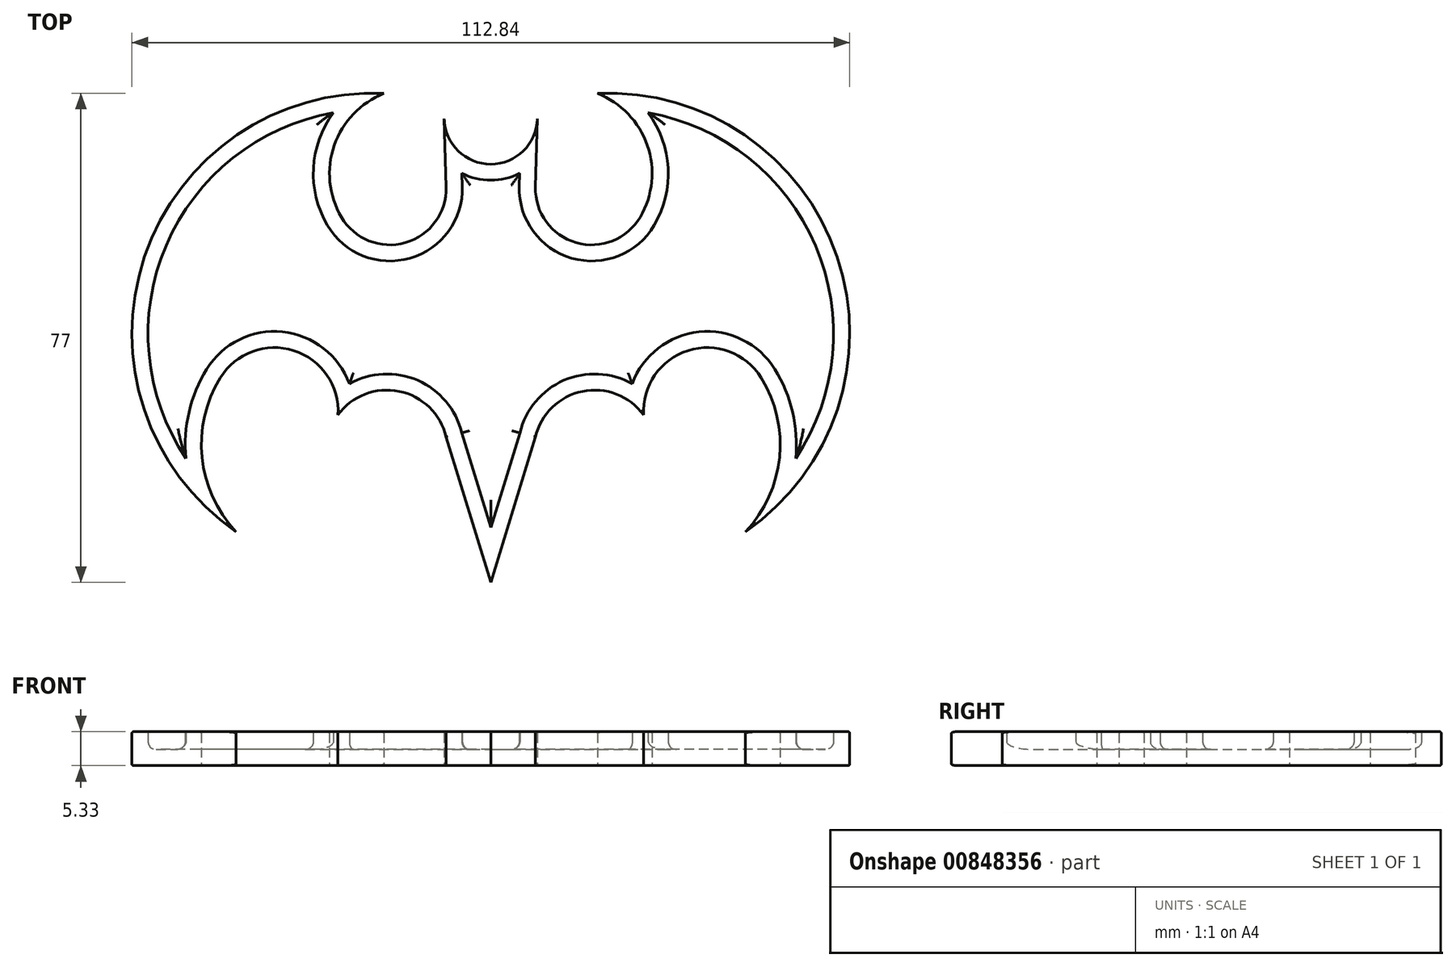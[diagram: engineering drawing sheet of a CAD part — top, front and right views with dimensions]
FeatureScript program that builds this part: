
annotation { "Feature Type Name" : "Feature", "Feature Type Description" : "" }
export const myFeature = defineFeature(function(context is Context, id is Id, definition is map)
    precondition{}
    {
        {
            var Q0;
            Q0=qCreatedBy(makeId("Top.planeOp"),FACE);
            var sketch = newSketch(context, id + "F0", { "sketchPlane" : qUnion([Q0])});
            skArc(sketch, "E0", {"start": v(-7.33, 18.25) * mm, "mid": v(-5.1, 13.2) * mm, "end": v(0, 11.13) * mm});
            skLineSegment(sketch, "E1", {"start": v(-7.33, 18.25) * mm, "end": v(-7.02, 7.53) * mm});
            skArc(sketch, "E2", {"start": v(-7.02, 7.53) * mm, "mid": v(-13.42, -1.23) * mm, "end": v(-23.5, 2.8) * mm});
            skArc(sketch, "E3", {"start": v(-23.5, 2.8) * mm, "mid": v(-24.61, 14.07) * mm, "end": v(-16.78, 22.26) * mm});
            skArc(sketch, "E4", {"start": v(-16.78, 22.26) * mm, "mid": v(-54.44, -3.46) * mm, "end": v(-40.04, -46.73) * mm});
            skArc(sketch, "E5", {"start": v(-42.5, -22.49) * mm, "mid": v(-45.4, -35.02) * mm, "end": v(-40.04, -46.73) * mm});
            skPoint(sketch, "E6.third.point", {"position": v(-25.5, -22.49) * mm});
            skLineSegment(sketch, "E7", {"start": v(-7.02, 7.53) * mm, "end": v(-7.02, 7.02) * mm, "construction": true});
            skArc(sketch, "E8", {"start": v(-7.02, -31.83) * mm, "mid": v(-14.4, -24.63) * mm, "end": v(-24.03, -28.35) * mm});
            skPoint(sketch, "E8.second.point", {"position": v(-7.02, -36.13) * mm});
            skPoint(sketch, "E8.third.point", {"position": v(-15.86, -43.52) * mm});
            skFitSpline(sketch, "E9", {"points": [v(-7.02, -31.83) * mm, v(0, -54.7) * mm], "startDerivative": vector(7.02, -22.88) * mm, "endDerivative": vector(7.02, -22.88) * mm});
            skArc(sketch, "E10.trimOffspring", {"start": v(-24.03, -28.35) * mm, "mid": v(-30.98, -18.22) * mm, "end": v(-42.5, -22.49) * mm});
            skPoint(sketch, "E11", {"position": v(0, 11.13) * mm});
            skArc(sketch, "E12.MirrorCS", {"start": v(7.33, 18.25) * mm, "mid": v(5.1, 13.2) * mm, "end": v(0, 11.13) * mm});
            skLineSegment(sketch, "E13.MirrorCS", {"start": v(7.33, 18.25) * mm, "end": v(7.02, 7.53) * mm});
            skArc(sketch, "E14.MirrorCS", {"start": v(7.02, 7.53) * mm, "mid": v(13.42, -1.23) * mm, "end": v(23.5, 2.8) * mm});
            skArc(sketch, "E15.MirrorCS", {"start": v(23.5, 2.8) * mm, "mid": v(24.61, 14.07) * mm, "end": v(16.78, 22.26) * mm});
            skArc(sketch, "E16.MirrorCS", {"start": v(16.78, 22.26) * mm, "mid": v(54.44, -3.46) * mm, "end": v(40.04, -46.73) * mm});
            skArc(sketch, "E17.MirrorCS", {"start": v(42.5, -22.49) * mm, "mid": v(45.4, -35.02) * mm, "end": v(40.04, -46.73) * mm});
            skArc(sketch, "E18.MirrorCS", {"start": v(24.03, -28.35) * mm, "mid": v(30.98, -18.22) * mm, "end": v(42.5, -22.49) * mm});
            skArc(sketch, "E19.MirrorCS", {"start": v(7.02, -31.83) * mm, "mid": v(14.4, -24.63) * mm, "end": v(24.03, -28.35) * mm});
            skFitSpline(sketch, "E20.MirrorCS", {"points": [v(7.02, -31.83) * mm, v(0, -54.7) * mm], "startDerivative": vector(-7.02, -22.88) * mm, "endDerivative": vector(-7.02, -22.88) * mm});
            skPoint(sketch, "E21.orphan", {"position": v(-15.86, -1.58) * mm});
            skPoint(sketch, "E22.orphan", {"position": v(0, -28.3) * mm});
            skPoint(sketch, "E23.orphan", {"position": v(-7.02, -54.26) * mm});
            skPoint(sketch, "E24.end.orphan", {"position": v(-15.86, -54.26) * mm});
            skSolve(sketch);
        }
        {
            var Q0;
            Q0=qSketchRegion(id+"F0",true);
            extrude(context, id + "F1", {"entities" : qUnion([Q0]), "depth" : 5.33 * mm});
        }
        {
            var Q0;
            Q0=makeQuery(id+"F1.opExtrude","CAP_EDGE",EDGE,{"disambiguationData":[OSD([sQuery(id+"F0.wireOp",EDGE,"E10.trimOffspring")])],"isStart":false});
            var Q1;
            Q1=makeQuery(id+"F1.opExtrude","CAP_FACE",FACE,{"disambiguationData":[OSD([sQuery(id+"F0.wireOp",EDGE,"E0"),sQuery(id+"F0.wireOp",EDGE,"E1"),sQuery(id+"F0.wireOp",EDGE,"E2"),sQuery(id+"F0.wireOp",EDGE,"E3"),sQuery(id+"F0.wireOp",EDGE,"E4"),sQuery(id+"F0.wireOp",EDGE,"E5"),sQuery(id+"F0.wireOp",EDGE,"E8"),sQuery(id+"F0.wireOp",EDGE,"E9"),sQuery(id+"F0.wireOp",EDGE,"E10.trimOffspring"),sQuery(id+"F0.wireOp",EDGE,"E12.MirrorCS"),sQuery(id+"F0.wireOp",EDGE,"E13.MirrorCS"),sQuery(id+"F0.wireOp",EDGE,"E14.MirrorCS"),sQuery(id+"F0.wireOp",EDGE,"E15.MirrorCS"),sQuery(id+"F0.wireOp",EDGE,"E16.MirrorCS"),sQuery(id+"F0.wireOp",EDGE,"E17.MirrorCS"),sQuery(id+"F0.wireOp",EDGE,"E18.MirrorCS"),sQuery(id+"F0.wireOp",EDGE,"E19.MirrorCS"),sQuery(id+"F0.wireOp",EDGE,"E20.MirrorCS")])],"isStart":false});
            fillet(context, id + "F2", {"entities" : qUnion([Q0, Q1]), "radius" : 0.25 * mm, "tangentPropagation" : true, "allowEdgeOverflow" : false});
        }
        {
            var Q0;
            Q0=makeQuery(id+"F1.opExtrude","CAP_FACE",FACE,{"disambiguationData":[OSD([sQuery(id+"F0.wireOp",EDGE,"E0"),sQuery(id+"F0.wireOp",EDGE,"E1"),sQuery(id+"F0.wireOp",EDGE,"E2"),sQuery(id+"F0.wireOp",EDGE,"E3"),sQuery(id+"F0.wireOp",EDGE,"E4"),sQuery(id+"F0.wireOp",EDGE,"E5"),sQuery(id+"F0.wireOp",EDGE,"E8"),sQuery(id+"F0.wireOp",EDGE,"E9"),sQuery(id+"F0.wireOp",EDGE,"E10.trimOffspring"),sQuery(id+"F0.wireOp",EDGE,"E12.MirrorCS"),sQuery(id+"F0.wireOp",EDGE,"E13.MirrorCS"),sQuery(id+"F0.wireOp",EDGE,"E14.MirrorCS"),sQuery(id+"F0.wireOp",EDGE,"E15.MirrorCS"),sQuery(id+"F0.wireOp",EDGE,"E16.MirrorCS"),sQuery(id+"F0.wireOp",EDGE,"E17.MirrorCS"),sQuery(id+"F0.wireOp",EDGE,"E18.MirrorCS"),sQuery(id+"F0.wireOp",EDGE,"E19.MirrorCS"),sQuery(id+"F0.wireOp",EDGE,"E20.MirrorCS")])],"isStart":true});
            fillet(context, id + "F3", {"entities" : qUnion([Q0]), "radius" : 0.25 * mm, "tangentPropagation" : true, "allowEdgeOverflow" : false});
        }
        {
            var Q0;
            Q0=makeQuery(id+"F1.opExtrude","CAP_FACE",FACE,{"disambiguationData":[OSD([sQuery(id+"F0.wireOp",EDGE,"E0"),sQuery(id+"F0.wireOp",EDGE,"E1"),sQuery(id+"F0.wireOp",EDGE,"E2"),sQuery(id+"F0.wireOp",EDGE,"E3"),sQuery(id+"F0.wireOp",EDGE,"E4"),sQuery(id+"F0.wireOp",EDGE,"E5"),sQuery(id+"F0.wireOp",EDGE,"E8"),sQuery(id+"F0.wireOp",EDGE,"E9"),sQuery(id+"F0.wireOp",EDGE,"E10.trimOffspring"),sQuery(id+"F0.wireOp",EDGE,"E12.MirrorCS"),sQuery(id+"F0.wireOp",EDGE,"E13.MirrorCS"),sQuery(id+"F0.wireOp",EDGE,"E14.MirrorCS"),sQuery(id+"F0.wireOp",EDGE,"E15.MirrorCS"),sQuery(id+"F0.wireOp",EDGE,"E16.MirrorCS"),sQuery(id+"F0.wireOp",EDGE,"E17.MirrorCS"),sQuery(id+"F0.wireOp",EDGE,"E18.MirrorCS"),sQuery(id+"F0.wireOp",EDGE,"E19.MirrorCS"),sQuery(id+"F0.wireOp",EDGE,"E20.MirrorCS")])],"isStart":false});
            shell(context, id + "F4", {"entities" : qUnion([Q0]), "thickness" : 2.54 * mm});
        }
        {
            var Q0;
            {var subQ0=sQuery(id+"F0.wireOp",EDGE,"E3");var subQ1=makeQuery(id+"F1.opExtrude","CAP_EDGE",EDGE,{"disambiguationData":[OSD([subQ0])],"isStart":true});var subQ2=sQuery(id+"F0.wireOp",EDGE,"E20.MirrorCS");var subQ3=sQuery(id+"F0.wireOp",EDGE,"E19.MirrorCS");var subQ4=sQuery(id+"F0.wireOp",EDGE,"E18.MirrorCS");var subQ5=sQuery(id+"F0.wireOp",EDGE,"E17.MirrorCS");var subQ6=sQuery(id+"F0.wireOp",EDGE,"E16.MirrorCS");var subQ7=sQuery(id+"F0.wireOp",EDGE,"E15.MirrorCS");var subQ8=sQuery(id+"F0.wireOp",EDGE,"E14.MirrorCS");var subQ9=sQuery(id+"F0.wireOp",EDGE,"E13.MirrorCS");var subQ10=sQuery(id+"F0.wireOp",EDGE,"E12.MirrorCS");var subQ11=sQuery(id+"F0.wireOp",EDGE,"E10.trimOffspring");var subQ12=sQuery(id+"F0.wireOp",EDGE,"E9");var subQ13=sQuery(id+"F0.wireOp",EDGE,"E8");var subQ14=sQuery(id+"F0.wireOp",EDGE,"E5");var subQ15=sQuery(id+"F0.wireOp",EDGE,"E4");var subQ16=sQuery(id+"F0.wireOp",EDGE,"E2");var subQ17=sQuery(id+"F0.wireOp",EDGE,"E1");var subQ18=sQuery(id+"F0.wireOp",EDGE,"E0");Q0=makeQuery(id+"F4.opShell","OFFSET_EDGE",EDGE,{"disambiguationData":[OSD([subQ18,subQ17,subQ16,subQ0,subQ15,subQ14,subQ13,subQ12,subQ11,subQ10,subQ9,subQ8,subQ7,subQ6,subQ5,subQ4,subQ3,subQ2]),TDD([makeQuery(id+"F3.opFillet","BLEND_EDGE",EDGE,{"blendedFrom":[subQ1,makeQuery(id+"F1.opExtrude","CAP_FACE",FACE,{"disambiguationData":[OSD([subQ18,subQ17,subQ16,subQ0,subQ15,subQ14,subQ13,subQ12,subQ11,subQ10,subQ9,subQ8,subQ7,subQ6,subQ5,subQ4,subQ3,subQ2])],"isStart":true})],"blendedInto":[makeQuery(id+"F1.opExtrude","CAP_FACE",FACE,{"disambiguationData":[OSD([subQ18,subQ17,subQ16,subQ0,subQ15,subQ14,subQ13,subQ12,subQ11,subQ10,subQ9,subQ8,subQ7,subQ6,subQ5,subQ4,subQ3,subQ2])],"isStart":true})]}),makeQuery(id+"F3.opFillet","BLEND_EDGE",EDGE,{"blendedFrom":[subQ1,makeQuery(id+"F1.opExtrude","SWEPT_FACE",FACE,{"disambiguationData":[OSD([subQ0])]})],"blendedInto":[makeQuery(id+"F1.opExtrude","SWEPT_FACE",FACE,{"disambiguationData":[OSD([subQ0])]})]})])]});}
            var Q1;
            {var subQ0=sQuery(id+"F0.wireOp",EDGE,"E12.MirrorCS");var subQ1=sQuery(id+"F0.wireOp",EDGE,"E0");var subQ2=makeQuery(id+"F1.opExtrude","CAP_EDGE",EDGE,{"disambiguationData":[OSD([subQ1,subQ0])],"isStart":true});var subQ3=sQuery(id+"F0.wireOp",EDGE,"E20.MirrorCS");var subQ4=sQuery(id+"F0.wireOp",EDGE,"E19.MirrorCS");var subQ5=sQuery(id+"F0.wireOp",EDGE,"E18.MirrorCS");var subQ6=sQuery(id+"F0.wireOp",EDGE,"E17.MirrorCS");var subQ7=sQuery(id+"F0.wireOp",EDGE,"E16.MirrorCS");var subQ8=sQuery(id+"F0.wireOp",EDGE,"E15.MirrorCS");var subQ9=sQuery(id+"F0.wireOp",EDGE,"E14.MirrorCS");var subQ10=sQuery(id+"F0.wireOp",EDGE,"E13.MirrorCS");var subQ11=sQuery(id+"F0.wireOp",EDGE,"E10.trimOffspring");var subQ12=sQuery(id+"F0.wireOp",EDGE,"E9");var subQ13=sQuery(id+"F0.wireOp",EDGE,"E8");var subQ14=sQuery(id+"F0.wireOp",EDGE,"E5");var subQ15=sQuery(id+"F0.wireOp",EDGE,"E4");var subQ16=sQuery(id+"F0.wireOp",EDGE,"E3");var subQ17=sQuery(id+"F0.wireOp",EDGE,"E2");var subQ18=sQuery(id+"F0.wireOp",EDGE,"E1");Q1=makeQuery(id+"F4.opShell","OFFSET_EDGE",EDGE,{"disambiguationData":[OSD([subQ1,subQ18,subQ17,subQ16,subQ15,subQ14,subQ13,subQ12,subQ11,subQ0,subQ10,subQ9,subQ8,subQ7,subQ6,subQ5,subQ4,subQ3]),TDD([makeQuery(id+"F3.opFillet","BLEND_EDGE",EDGE,{"blendedFrom":[subQ2,makeQuery(id+"F1.opExtrude","CAP_FACE",FACE,{"disambiguationData":[OSD([subQ1,subQ18,subQ17,subQ16,subQ15,subQ14,subQ13,subQ12,subQ11,subQ0,subQ10,subQ9,subQ8,subQ7,subQ6,subQ5,subQ4,subQ3])],"isStart":true})],"blendedInto":[makeQuery(id+"F1.opExtrude","CAP_FACE",FACE,{"disambiguationData":[OSD([subQ1,subQ18,subQ17,subQ16,subQ15,subQ14,subQ13,subQ12,subQ11,subQ0,subQ10,subQ9,subQ8,subQ7,subQ6,subQ5,subQ4,subQ3])],"isStart":true})]}),makeQuery(id+"F3.opFillet","BLEND_EDGE",EDGE,{"blendedFrom":[subQ2,makeQuery(id+"F1.opExtrude","SWEPT_FACE",FACE,{"disambiguationData":[OSD([subQ1,subQ0])]})],"blendedInto":[makeQuery(id+"F1.opExtrude","SWEPT_FACE",FACE,{"disambiguationData":[OSD([subQ1,subQ0])]})]})])]});}
            var Q2;
            Q2=makeQuery(id+"F4.opShell","OFFSET_FACE",FACE,{"disambiguationData":[OSD([sQuery(id+"F0.wireOp",EDGE,"E0"),sQuery(id+"F0.wireOp",EDGE,"E1"),sQuery(id+"F0.wireOp",EDGE,"E2"),sQuery(id+"F0.wireOp",EDGE,"E3"),sQuery(id+"F0.wireOp",EDGE,"E4"),sQuery(id+"F0.wireOp",EDGE,"E5"),sQuery(id+"F0.wireOp",EDGE,"E8"),sQuery(id+"F0.wireOp",EDGE,"E9"),sQuery(id+"F0.wireOp",EDGE,"E10.trimOffspring"),sQuery(id+"F0.wireOp",EDGE,"E12.MirrorCS"),sQuery(id+"F0.wireOp",EDGE,"E13.MirrorCS"),sQuery(id+"F0.wireOp",EDGE,"E14.MirrorCS"),sQuery(id+"F0.wireOp",EDGE,"E15.MirrorCS"),sQuery(id+"F0.wireOp",EDGE,"E16.MirrorCS"),sQuery(id+"F0.wireOp",EDGE,"E17.MirrorCS"),sQuery(id+"F0.wireOp",EDGE,"E18.MirrorCS"),sQuery(id+"F0.wireOp",EDGE,"E19.MirrorCS"),sQuery(id+"F0.wireOp",EDGE,"E20.MirrorCS")])]});
            fillet(context, id + "F5", {"entities" : qUnion([Q0, Q1, Q2]), "radius" : 1.27 * mm, "tangentPropagation" : true, "allowEdgeOverflow" : false});
        }
    });
